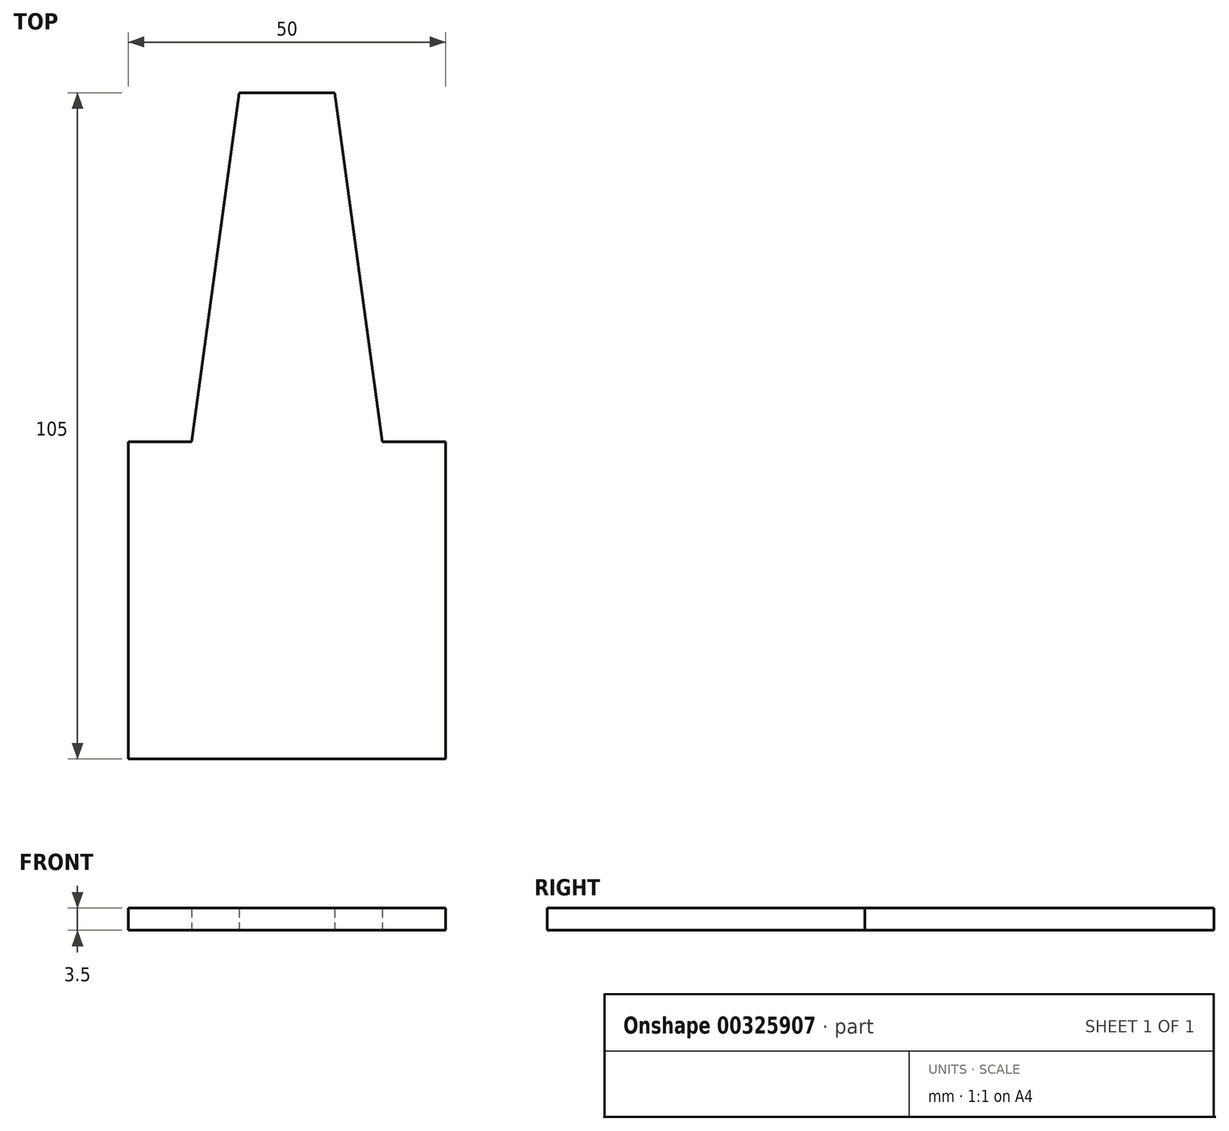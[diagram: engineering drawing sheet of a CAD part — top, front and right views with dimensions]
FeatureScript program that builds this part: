
annotation { "Feature Type Name" : "Feature", "Feature Type Description" : "" }
export const myFeature = defineFeature(function(context is Context, id is Id, definition is map)
    precondition{}
    {
        {
            var Q0;
            Q0=qCreatedBy(makeId("Top.planeOp"),FACE);
            var sketch = newSketch(context, id + "F0", { "sketchPlane" : qUnion([Q0])});
            skLineSegment(sketch, "E0.bottom", {"start": v(25, -25) * mm, "end": v(-25, -25) * mm});
            skLineSegment(sketch, "E0.top", {"start": v(25, 25) * mm, "end": v(-25, 25) * mm});
            skLineSegment(sketch, "E0.left", {"start": v(25, -25) * mm, "end": v(25, 25) * mm});
            skLineSegment(sketch, "E0.right", {"start": v(-25, -25) * mm, "end": v(-25, 25) * mm});
            skPoint(sketch, "E0.middle", {"position": v(0, 0) * mm});
            skLineSegment(sketch, "E1", {"start": v(-15, 25) * mm, "end": v(-7.5, 80) * mm});
            skLineSegment(sketch, "E2", {"start": v(-7.5, 80) * mm, "end": v(7.5, 80) * mm});
            skLineSegment(sketch, "E3", {"start": v(7.5, 80) * mm, "end": v(15, 25) * mm});
            skSolve(sketch);
        }
        {
            var Q0;
            Q0=makeQuery(id+"F0.imprint","IMPRINT",FACE,{"disambiguationData":[TD([[makeQuery(id+"F0.imprint","IMPRINT",EDGE,{"derivedFrom":sQuery(id+"F0.wireOp",EDGE,"E0.bottom")}),-1.0]])]});
            var Q1;
            {var subQ0=sQuery(id+"F0.wireOp",EDGE,"E1");Q1=makeQuery(id+"F0.imprint","IMPRINT",FACE,{"disambiguationData":[TD([[makeQuery(id+"F0.imprint","IMPRINT",EDGE,{"derivedFrom":subQ0}),-1.0]])]});}
            extrude(context, id + "F1", {"entities" : qUnion([Q0, Q1]), "depth" : 3.5 * mm});
        }
    });
